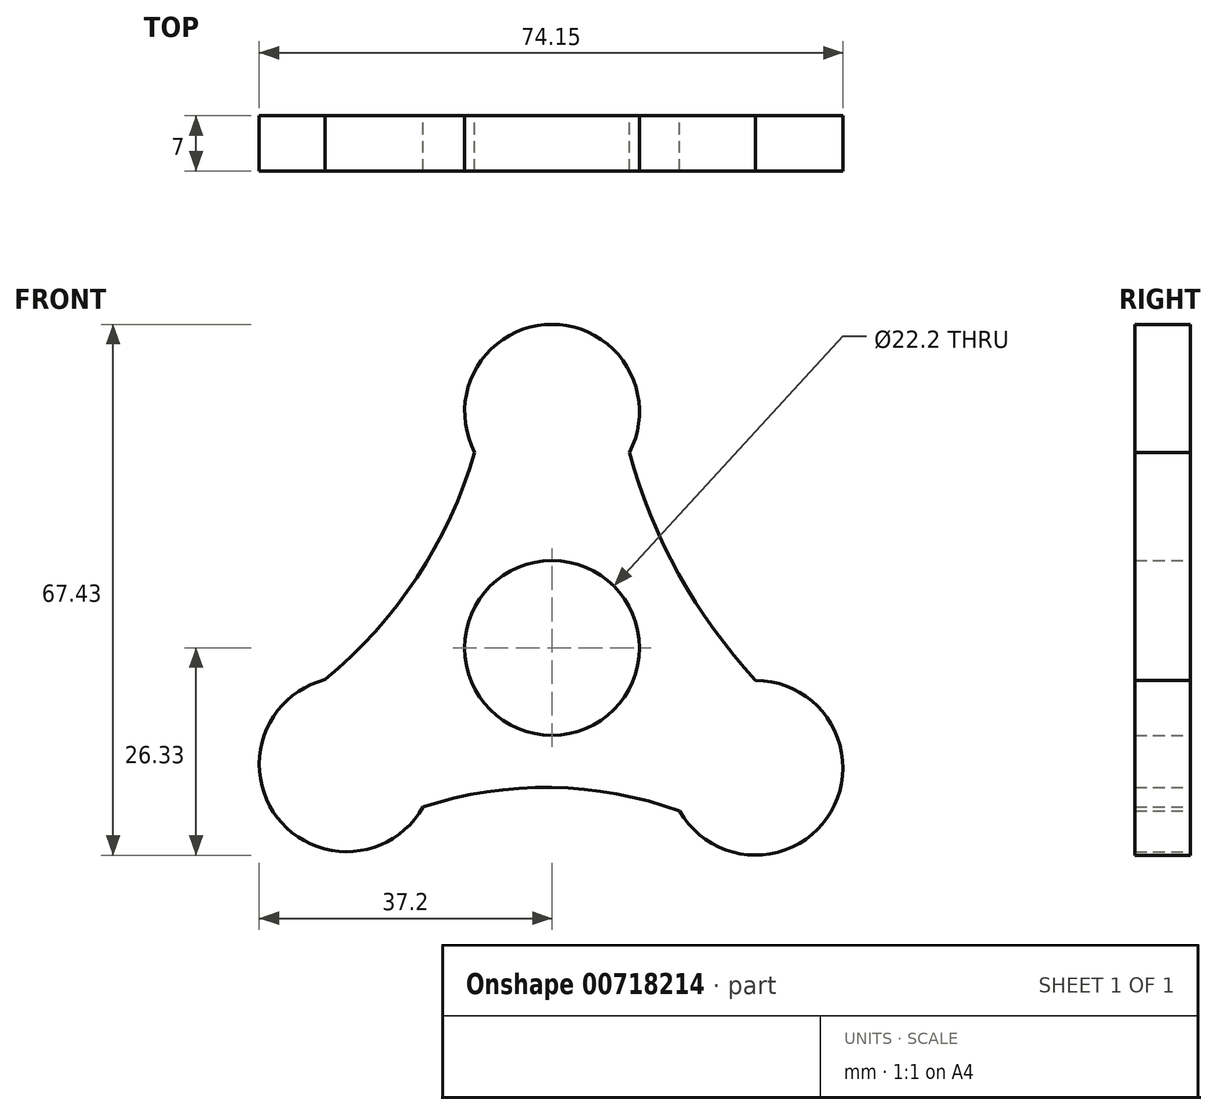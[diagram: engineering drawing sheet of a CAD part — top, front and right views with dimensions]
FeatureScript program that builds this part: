
annotation { "Feature Type Name" : "Feature", "Feature Type Description" : "" }
export const myFeature = defineFeature(function(context is Context, id is Id, definition is map)
    precondition{}
    {
        {
            var Q0;
            Q0=qCreatedBy(makeId("Front.planeOp"),FACE);
            var sketch = newSketch(context, id + "F0", { "sketchPlane" : qUnion([Q0])});
            skCircle(sketch, "E0", {"center": v(0, 0) * mm, "radius": 11.1 * mm});
            skCircle(sketch, "E1", {"center": v(0, 30) * mm, "radius": 11.1 * mm});
            skCircle(sketch, "E2", {"center": v(25.85, -15.23) * mm, "radius": 11.1 * mm});
            skCircle(sketch, "E3", {"center": v(-26.1, -14.8) * mm, "radius": 11.1 * mm});
            skArc(sketch, "E4", {"start": v(-28.85, -4.04) * mm, "mid": v(-17.17, 8.97) * mm, "end": v(-9.83, 24.83) * mm});
            skArc(sketch, "E5", {"start": v(9.83, 24.83) * mm, "mid": v(16.09, 9.38) * mm, "end": v(25.87, -4.13) * mm});
            skArc(sketch, "E6", {"start": v(16.2, -20.74) * mm, "mid": v(-0.06, -17.73) * mm, "end": v(-16.42, -20.22) * mm});
            skSolve(sketch);
        }
        {
            var Q0;
            Q0 = qSketchRegion(id + "F0", true);
            extrude(context, id + "F1", {"entities" : qUnion([Q0]), "depth" : 7 * mm, "offsetDistance" : 25 * mm});
        }
        {
            var Q0;
            Q0 = qSketchRegion(id + "F0", true);
            extrude(context, id + "F2", {"entities" : qUnion([Q0]), "operationType" : NewBodyOperationType.ADD, "depth" : 7 * mm, "offsetDistance" : 25 * mm});
        }
        {
            var Q0;
            Q0 = qSketchRegion(id + "F0", true);
            extrude(context, id + "F3", {"entities" : qUnion([Q0]), "operationType" : NewBodyOperationType.ADD, "depth" : 5 * mm, "offsetDistance" : 25 * mm});
        }
    });
